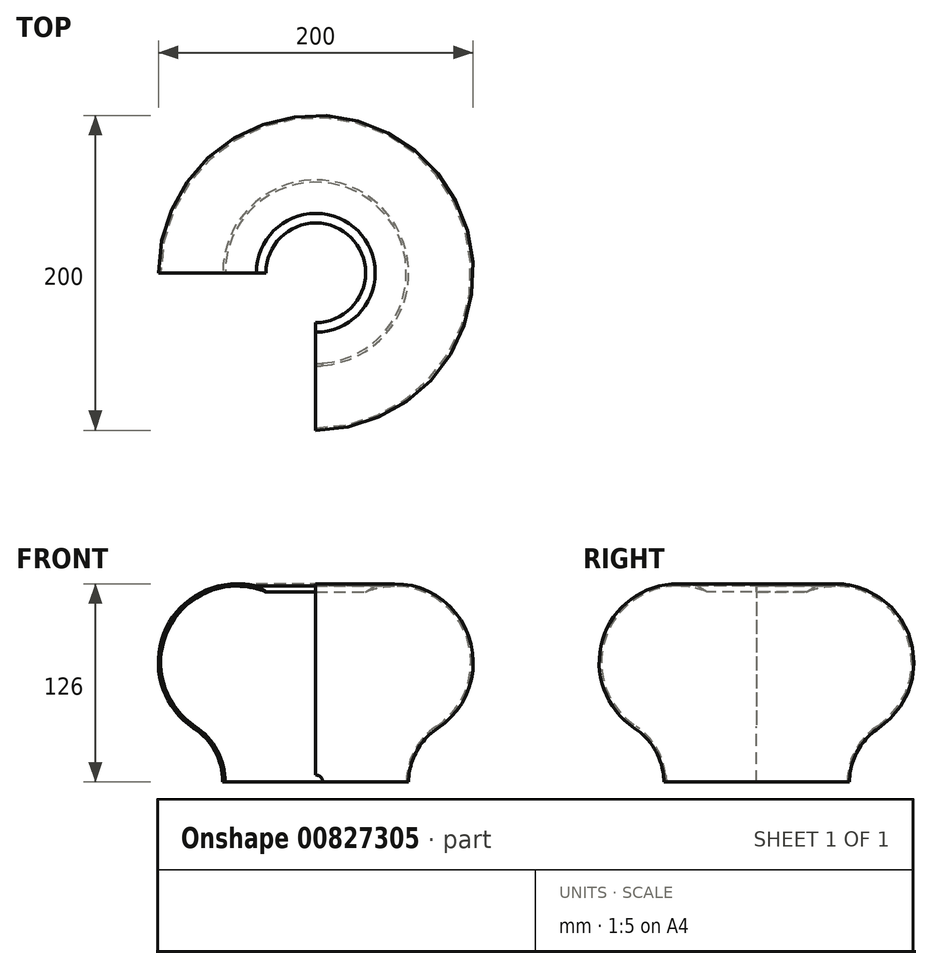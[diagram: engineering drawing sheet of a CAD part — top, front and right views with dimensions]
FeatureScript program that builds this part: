
annotation { "Feature Type Name" : "Feature", "Feature Type Description" : "" }
export const myFeature = defineFeature(function(context is Context, id is Id, definition is map)
    precondition{}
    {
        {
            var Q0;
            Q0=qCreatedBy(makeId("Right.planeOp"),FACE);
            var sketch = newSketch(context, id + "F0", { "sketchPlane" : qUnion([Q0])});
            skPoint(sketch, "E0", {"position": v(0, 76) * mm});
            skPoint(sketch, "E1", {"position": v(-50, 76) * mm});
            skArc(sketch, "E2", {"start": v(0, 98.5) * mm, "mid": v(-22.5, 76) * mm, "end": v(0, 53.5) * mm});
            skLineSegment(sketch, "E3.trimOffspring", {"start": v(0, 53.5) * mm, "end": v(0, 98.5) * mm});
            skArc(sketch, "E4", {"start": v(-31.66, 120.9) * mm, "mid": v(-92.91, 98.6) * mm, "end": v(-76.66, 35.48) * mm});
            skArc(sketch, "E5.trimOffspring", {"start": v(-37.75, 124.47) * mm, "mid": v(-95.76, 96.15) * mm, "end": v(-77.48, 34.23) * mm});
            skLineSegment(sketch, "E6", {"start": v(-31.66, 120.9) * mm, "end": v(-37.75, 124.47) * mm});
            skPoint(sketch, "E7", {"position": v(-100, 0) * mm});
            skPoint(sketch, "E8", {"position": v(-59.03, 0) * mm});
            skPoint(sketch, "E9", {"position": v(-57.53, 0) * mm});
            skLineSegment(sketch, "E10", {"start": v(-59.03, 0) * mm, "end": v(-57.53, 0) * mm});
            skArc(sketch, "E11", {"start": v(-57.53, 0) * mm, "mid": v(-62.61, 20.16) * mm, "end": v(-76.66, 35.48) * mm});
            skArc(sketch, "E12", {"start": v(-59.03, 0) * mm, "mid": v(-63.93, 19.44) * mm, "end": v(-77.48, 34.23) * mm});
            skSolve(sketch);
        }
        {
            var Q0;
            Q0=makeQuery(id+"F0.imprint","IMPRINT",FACE,{"disambiguationData":[TD([[makeQuery(id+"F0.imprint","IMPRINT",EDGE,{"derivedFrom":sQuery(id+"F0.wireOp",EDGE,"dad85534-1b68-4845-88fe-fa06ed893c96")}),-1.0]])]});
            var Q1;
            Q1=makeQuery(id+"F0.imprint","IMPRINT",FACE,{"disambiguationData":[TD([[makeQuery(id+"F0.imprint","IMPRINT",EDGE,{"derivedFrom":sQuery(id+"F0.wireOp",EDGE,"E5.trimOffspring")}),1.0]])]});
            var Q2;
            Q2=sQuery(id+"F0.wireOp",EDGE,"E3.trimOffspring");
            revolve(context, id + "F1", {"surfaceOperationType" : NewSurfaceOperationType.NEW, "entities" : qUnion([Q0, Q1]), "axis" : qUnion([Q2]), "revolveType" : RevolveType.ONE_DIRECTION, "angle" : 270 * degree});
        }
        {
            var Q0;
            Q0=qCreatedBy(makeId("Front.planeOp"),FACE);
            var sketch = newSketch(context, id + "F2", { "sketchPlane" : qUnion([Q0])});
            skArc(sketch, "E13", {"start": v(4.5, 0) * mm, "mid": v(0, 4.5) * mm, "end": v(-4.5, 0) * mm});
            skLineSegment(sketch, "E14.bottom", {"start": v(-4.5, 0) * mm, "end": v(4.5, 0) * mm});
            skLineSegment(sketch, "E14.top", {"start": v(-4.5, 0) * mm, "end": v(4.5, 0) * mm});
            skLineSegment(sketch, "E14.left", {"start": v(-4.5, 0) * mm, "end": v(-4.5, 0) * mm});
            skLineSegment(sketch, "E14.right", {"start": v(4.5, 0) * mm, "end": v(4.5, 0) * mm});
            skSolve(sketch);
        }
        {
            var Q0;
            Q0 = qSketchRegion(id + "F2", true);
            extrude(context, id + "F3", {"entities" : qUnion([Q0]), "operationType" : NewBodyOperationType.REMOVE, "endBound" : BoundingType.THROUGH_ALL, "depth" : 60.2 * mm, "offsetDistance" : 25 * mm});
        }
    });
